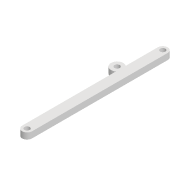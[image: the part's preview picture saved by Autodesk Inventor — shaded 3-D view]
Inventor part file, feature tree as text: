
AUTODESK INVENTOR PART (.ipt)
format: ipt  version: 2022 (Build 260153000, 153)  size: 98,304 bytes
history: native  units: mm
features: extrude x1, sketch x1
ambient origin geometry x8: Origin, YZ Plane, XZ Plane, XY Plane, X Axis, Y Axis, Z Axis, Center Point
bodies: Solid1 (feature_tree)
feature tree (2):
  extrude  "Extrusion1"  Depth=8.0mm
  sketch  "Sketch1"  dims[d0=110.0mm d1=8.0mm d2=4.2mm d3=4.2mm d4=5.0mm d5=0.0mm d6=4.2mm d9=80.0mm d10=3.0mm d11=10.0mm]
